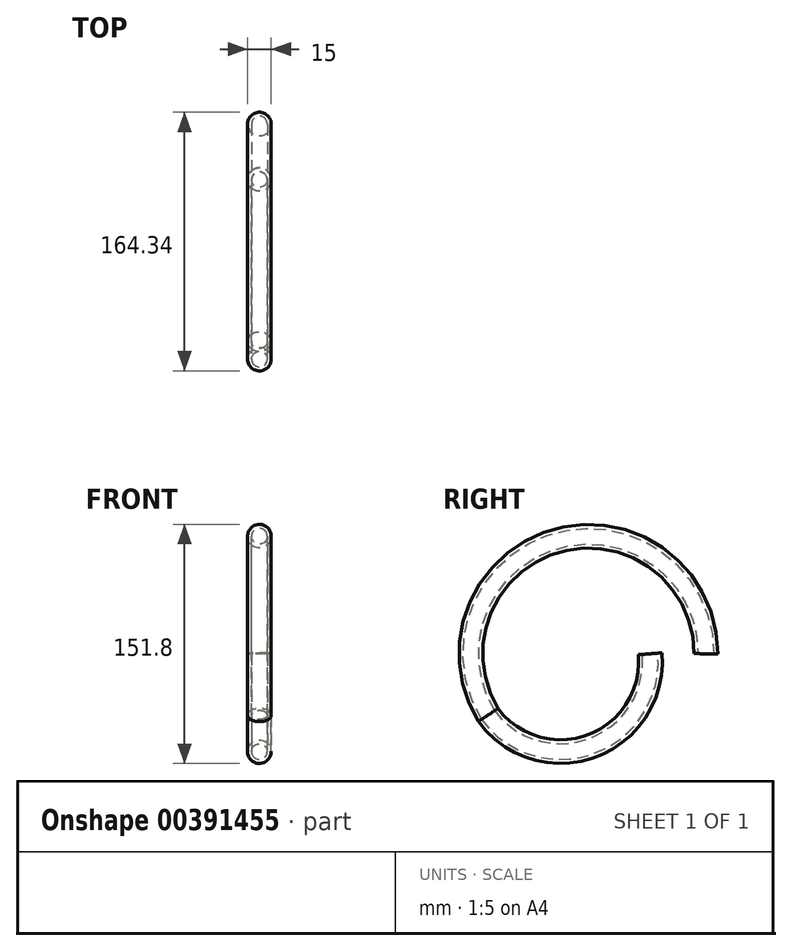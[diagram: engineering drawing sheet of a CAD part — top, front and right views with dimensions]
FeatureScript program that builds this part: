
annotation { "Feature Type Name" : "Feature", "Feature Type Description" : "" }
export const myFeature = defineFeature(function(context is Context, id is Id, definition is map)
    precondition{}
    {
        {
            var Q0;
            Q0=qCreatedBy(makeId("Right.planeOp"),FACE);
            var sketch = newSketch(context, id + "F0", { "sketchPlane" : qUnion([Q0])});
            skArc(sketch, "E0.0", {"start": v(54.86, 38.41) * mm, "mid": v(-37.24, 55.38) * mm, "end": v(-57.65, -36.02) * mm});
            skLineSegment(sketch, "E1", {"start": v(0, 0) * mm, "end": v(-57.65, -36.02) * mm, "construction": true});
            skLineSegment(sketch, "E2", {"start": v(-57.65, -36.02) * mm, "end": v(-70.37, -43.97) * mm, "construction": true});
            skLineSegment(sketch, "E3", {"start": v(0, 0) * mm, "end": v(43, 30.11) * mm, "construction": true});
            skLineSegment(sketch, "E4", {"start": v(43, 30.11) * mm, "end": v(72.26, 50.6) * mm, "construction": true});
            skLineSegment(sketch, "E5", {"start": v(0, 66.58) * mm, "end": v(0, -68.42) * mm, "construction": true});
            skLineSegment(sketch, "E6", {"start": v(0, -67.52) * mm, "end": v(0, -68.42) * mm, "construction": true});
            skArc(sketch, "E7", {"start": v(-57.65, -36.02) * mm, "mid": v(-56.93, -36.97) * mm, "end": v(-56.19, -37.9) * mm});
            skArc(sketch, "E8", {"start": v(-56.19, -37.9) * mm, "mid": v(1.58, -52.03) * mm, "end": v(32, -0.92) * mm});
            skLineSegment(sketch, "E9.trimOffspring", {"start": v(0, -75) * mm, "end": v(0, -76.84) * mm, "construction": true});
            skArc(sketch, "E10", {"start": v(-70.37, -43.97) * mm, "mid": v(4.61, -66.89) * mm, "end": v(47, -0.92) * mm});
            skLineSegment(sketch, "E11.trimOffspring", {"start": v(9.33, -47.95) * mm, "end": v(16.15, -61.3) * mm, "construction": true});
            skLineSegment(sketch, "E12.trimOffspring", {"start": v(21.46, -71.7) * mm, "end": v(21.5, -71.77) * mm, "construction": true});
            skPoint(sketch, "E13.trimOffspring.end.orphan", {"position": v(47, -0.92) * mm});
            skArc(sketch, "E14", {"start": v(67.5, -0.91) * mm, "mid": v(64.26, 19.74) * mm, "end": v(54.86, 38.41) * mm});
            skLineSegment(sketch, "E15", {"start": v(67.5, -0.91) * mm, "end": v(82.5, -0.91) * mm});
            skArc(sketch, "E16.trimOffspring", {"start": v(74.67, -0.91) * mm, "mid": v(-20.2, 70.96) * mm, "end": v(-63.73, -39.82) * mm});
            skArc(sketch, "E17", {"start": v(-63.73, -39.82) * mm, "mid": v(2.45, -59.36) * mm, "end": v(39.16, -0.92) * mm});
            skArc(sketch, "E18", {"start": v(82.5, -0.91) * mm, "mid": v(-22.37, 78.5) * mm, "end": v(-70.37, -43.97) * mm});
            skLineSegment(sketch, "E19", {"start": v(47, -0.92) * mm, "end": v(32, -0.92) * mm});
            skSolve(sketch);
        }
        {
            var Q0;
            Q0=qCreatedBy(makeId("Top.planeOp"),FACE);
            var sketch = newSketch(context, id + "F1", { "sketchPlane" : qUnion([Q0])});
            skCircle(sketch, "E20", {"center": v(0, 74.67) * mm, "radius": 7.5 * mm});
            skCircle(sketch, "E21", {"center": v(0, 74.67) * mm, "radius": 5 * mm});
            skSolve(sketch);
        }
        {
            var Q0;
            Q0=makeQuery(id+"F1.imprint","IMPRINT",FACE,{"disambiguationData":[TD([[makeQuery(id+"F1.imprint","IMPRINT",EDGE,{"derivedFrom":sQuery(id+"F1.wireOp",EDGE,"E20")}),1.0]])]});
            var Q1;
            Q1=sQuery(id+"F0.wireOp",EDGE,"E16.trimOffspring");
            var Q2;
            Q2=sQuery(id+"F0.wireOp",EDGE,"E17");
            sweep(context, id + "F2", {"profiles" : qUnion([Q0]), "path" : qUnion([Q1, Q2])});
        }
    });
